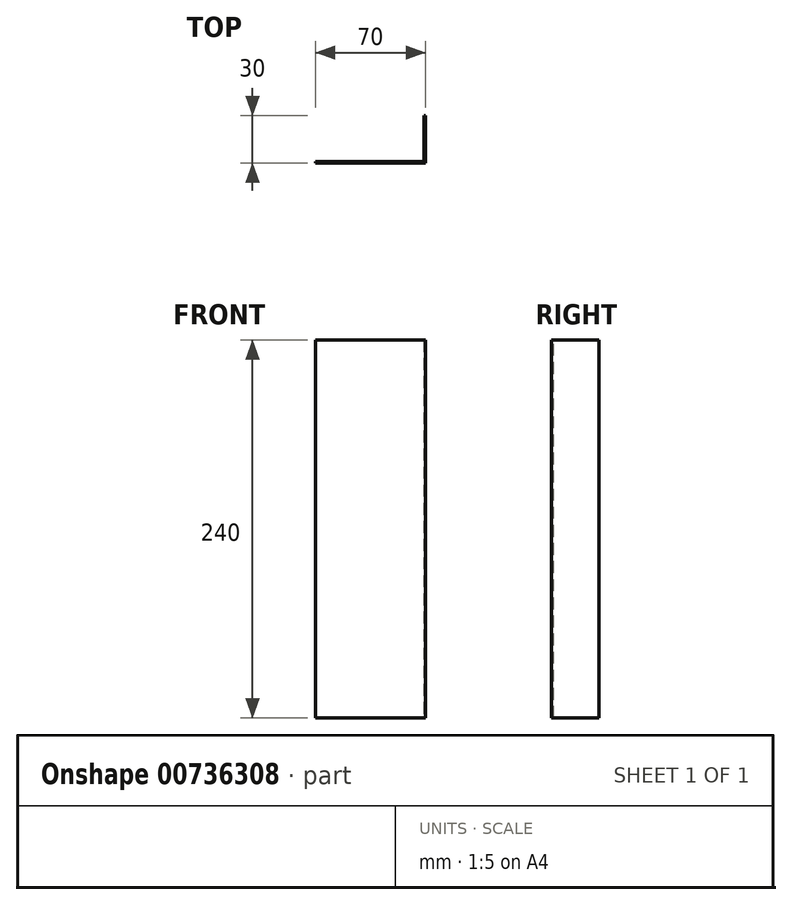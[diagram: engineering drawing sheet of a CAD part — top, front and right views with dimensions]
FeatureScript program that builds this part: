
annotation { "Feature Type Name" : "Feature", "Feature Type Description" : "" }
export const myFeature = defineFeature(function(context is Context, id is Id, definition is map)
    precondition{}
    {
        {
            var Q0;
            Q0=qCreatedBy(makeId("Front.planeOp"),FACE);
            var sketch = newSketch(context, id + "F0", { "sketchPlane" : qUnion([Q0])});
            skLineSegment(sketch, "E0.bottom", {"start": v(1.3, 0) * mm, "end": v(71.3, 0) * mm});
            skLineSegment(sketch, "E0.top", {"start": v(1.3, 240) * mm, "end": v(71.3, 240) * mm});
            skLineSegment(sketch, "E0.left", {"start": v(1.3, 0) * mm, "end": v(1.3, 240) * mm});
            skLineSegment(sketch, "E0.right", {"start": v(71.3, 0) * mm, "end": v(71.3, 240) * mm});
            skSolve(sketch);
        }
        {
            var Q0;
            Q0 = qSketchRegion(id + "F0", true);
            extrude(context, id + "F1", {"entities" : qUnion([Q0]), "depth" : 1 * mm, "offsetDistance" : 25 * mm});
        }
        {
            var Q0;
            Q0=makeQuery(id+"F1.opExtrude","CAP_FACE",FACE,{"disambiguationData":[OSD([sQuery(id+"F0.wireOp",EDGE,"E0.bottom"),sQuery(id+"F0.wireOp",EDGE,"E0.top"),sQuery(id+"F0.wireOp",EDGE,"E0.left"),sQuery(id+"F0.wireOp",EDGE,"E0.right")])],"isStart":true});
            var sketch = newSketch(context, id + "F2", { "sketchPlane" : qUnion([Q0])});
            skLineSegment(sketch, "E1.bottom", {"start": v(-71.3, 240) * mm, "end": v(-70.3, 240) * mm});
            skLineSegment(sketch, "E1.top", {"start": v(-71.3, 0) * mm, "end": v(-70.3, 0) * mm});
            skLineSegment(sketch, "E1.left", {"start": v(-71.3, 240) * mm, "end": v(-71.3, 0) * mm});
            skLineSegment(sketch, "E1.right", {"start": v(-70.3, 240) * mm, "end": v(-70.3, 0) * mm});
            skSolve(sketch);
        }
        {
            var Q0;
            Q0 = qSketchRegion(id + "F2", true);
            extrude(context, id + "F3", {"entities" : qUnion([Q0]), "operationType" : NewBodyOperationType.ADD, "depth" : 29 * mm, "offsetDistance" : 25 * mm});
        }
    });
